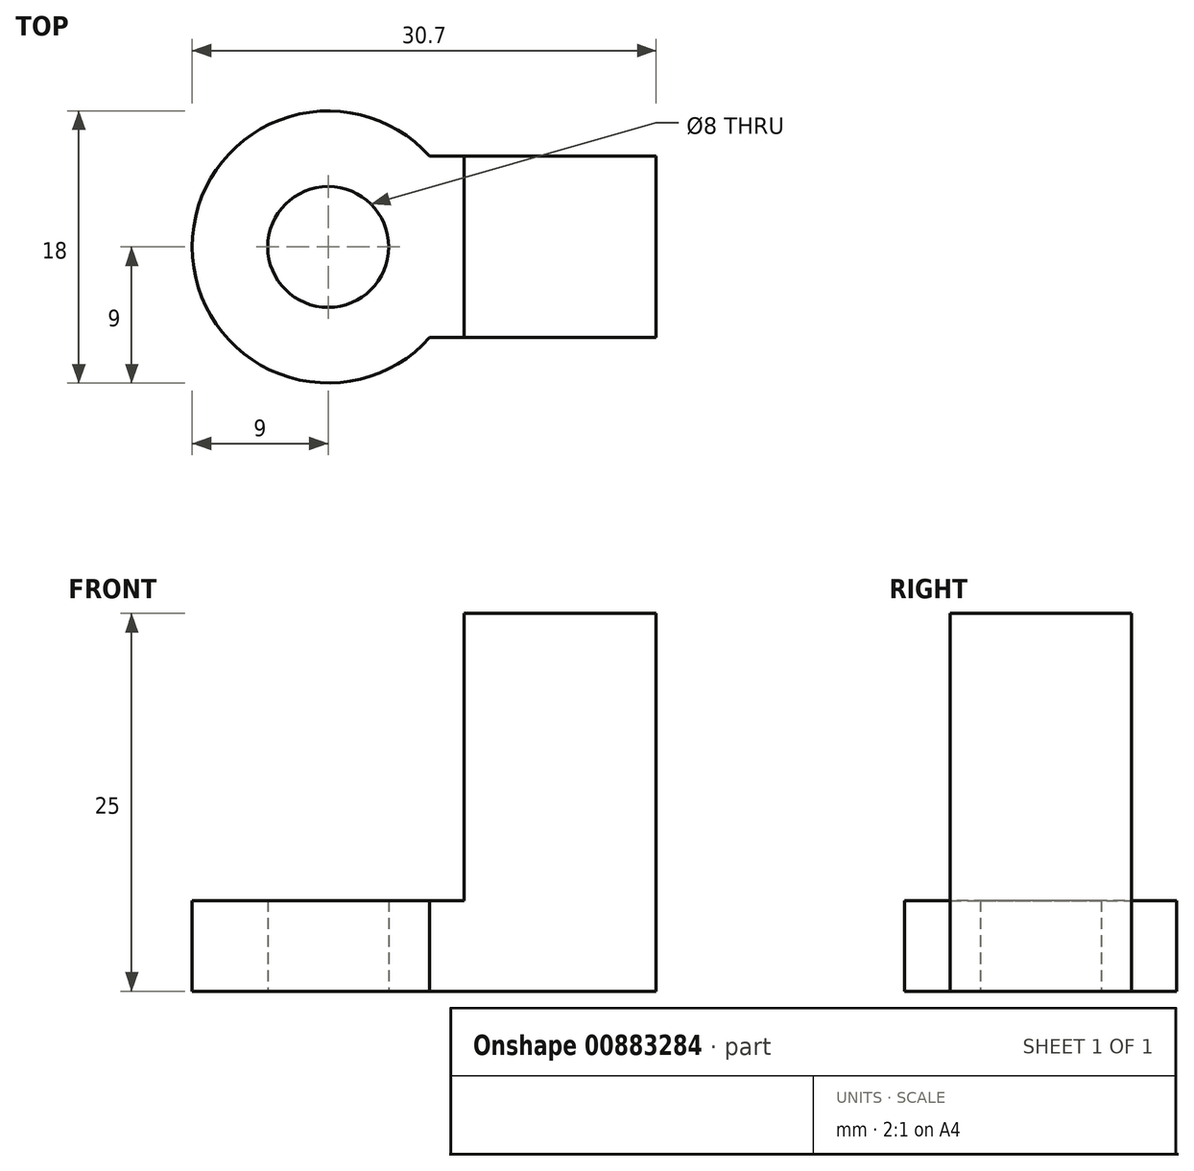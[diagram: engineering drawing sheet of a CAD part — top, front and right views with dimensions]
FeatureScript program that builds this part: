
annotation { "Feature Type Name" : "Feature", "Feature Type Description" : "" }
export const myFeature = defineFeature(function(context is Context, id is Id, definition is map)
    precondition{}
    {
        {
            var Q0;
            Q0=qCreatedBy(makeId("Top.planeOp"),FACE);
            var sketch = newSketch(context, id + "F0", { "sketchPlane" : qUnion([Q0])});
            skLineSegment(sketch, "E0", {"start": v(0, 0) * mm, "end": v(-12.7, 0) * mm});
            skCircle(sketch, "E1", {"center": v(-21.7, 0) * mm, "radius": 4 * mm});
            skLineSegment(sketch, "E2", {"start": v(0, 0) * mm, "end": v(12.7, 0) * mm});
            skLineSegment(sketch, "E3", {"start": v(0, 0) * mm, "end": v(0, 6) * mm});
            skLineSegment(sketch, "E4", {"start": v(0, 6) * mm, "end": v(0, -6) * mm});
            skLineSegment(sketch, "E5", {"start": v(0, -6) * mm, "end": v(-12.7, -6) * mm});
            skLineSegment(sketch, "E6", {"start": v(0, 6) * mm, "end": v(-12.7, 6) * mm});
            skLineSegment(sketch, "E7", {"start": v(0, 6) * mm, "end": v(12.7, 6) * mm});
            skLineSegment(sketch, "E8", {"start": v(12.7, 6) * mm, "end": v(12.7, -6) * mm});
            skLineSegment(sketch, "E9", {"start": v(12.7, -6) * mm, "end": v(0, -6) * mm});
            skLineSegment(sketch, "E10", {"start": v(12.7, -6) * mm, "end": v(7.7, -6) * mm});
            skLineSegment(sketch, "E11", {"start": v(7.7, -6) * mm, "end": v(7.7, -24) * mm});
            skLineSegment(sketch, "E12", {"start": v(7.7, -24) * mm, "end": v(12.7, -24) * mm});
            skLineSegment(sketch, "E13", {"start": v(12.7, -24) * mm, "end": v(12.7, -6) * mm});
            skCircle(sketch, "E14", {"center": v(-21.7, 0) * mm, "radius": 9 * mm});
            skLineSegment(sketch, "E15", {"start": v(-12.7, 6) * mm, "end": v(-15, 6) * mm});
            skLineSegment(sketch, "E16", {"start": v(-12.7, -6) * mm, "end": v(-15, -6) * mm});
            skLineSegment(sketch, "E17", {"start": v(-12.7, 0) * mm, "end": v(-12.7, 6) * mm});
            skLineSegment(sketch, "E18", {"start": v(-12.7, 0) * mm, "end": v(-12.7, -6) * mm});
            skSolve(sketch);
        }
        {
            var Q0;
            Q0=makeQuery(id+"F0.imprint","IMPRINT",FACE,{"disambiguationData":[TD([[makeQuery(id+"F0.imprint","IMPRINT",EDGE,{"derivedFrom":sQuery(id+"F0.wireOp",EDGE,"E1")}),-1.0]])]});
            extrude(context, id + "F1", {"entities" : qUnion([Q0]), "depth" : 6 * mm, "offsetDistance" : 25 * mm});
        }
        {
            var Q0;
            {var subQ2=sQuery(id+"F0.wireOp",EDGE,"E16");Q0=makeQuery(id+"F0.imprint","IMPRINT",FACE,{"disambiguationData":[TD([[makeQuery(id+"F0.imprint","IMPRINT",EDGE,{"derivedFrom":subQ2}),-1.0]])]});}
            var Q1;
            {var subQ2=sQuery(id+"F0.wireOp",EDGE,"E15");Q1=makeQuery(id+"F0.imprint","IMPRINT",FACE,{"disambiguationData":[TD([[makeQuery(id+"F0.imprint","IMPRINT",EDGE,{"derivedFrom":subQ2}),1.0]])]});}
            extrude(context, id + "F2", {"entities" : qUnion([Q0, Q1]), "operationType" : NewBodyOperationType.ADD, "depth" : 6 * mm, "offsetDistance" : 25 * mm});
        }
        {
            var Q0;
            Q0=makeQuery(id+"F0.imprint","IMPRINT",FACE,{"disambiguationData":[TD([[makeQuery(id+"F0.imprint","IMPRINT",EDGE,{"derivedFrom":sQuery(id+"F0.wireOp",EDGE,"E0")}),1.0]])]});
            var Q1;
            Q1=makeQuery(id+"F0.imprint","IMPRINT",FACE,{"disambiguationData":[TD([[makeQuery(id+"F0.imprint","IMPRINT",EDGE,{"derivedFrom":sQuery(id+"F0.wireOp",EDGE,"E0")}),-1.0]])]});
            extrude(context, id + "F3", {"entities" : qUnion([Q0, Q1]), "operationType" : NewBodyOperationType.ADD, "depth" : 25 * mm, "offsetDistance" : 25 * mm});
        }
    });
